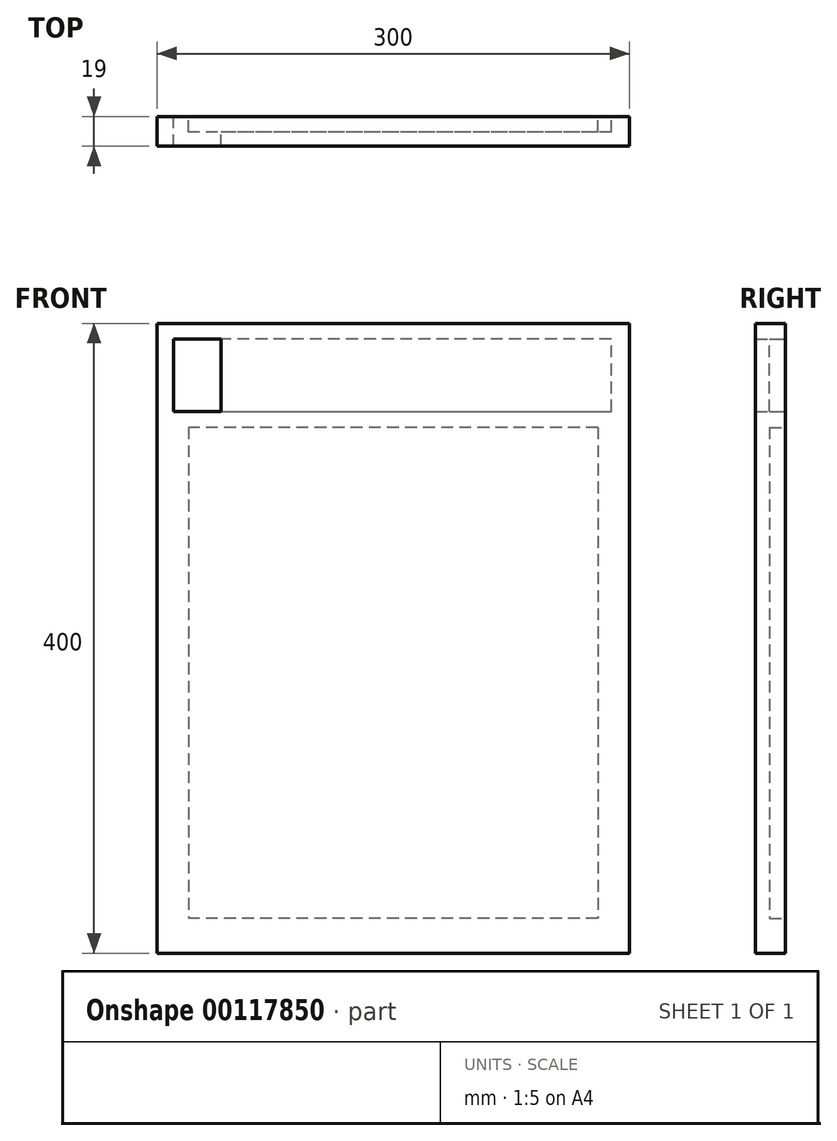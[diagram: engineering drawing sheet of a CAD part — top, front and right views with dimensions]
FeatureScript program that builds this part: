
annotation { "Feature Type Name" : "Feature", "Feature Type Description" : "" }
export const myFeature = defineFeature(function(context is Context, id is Id, definition is map)
    precondition{}
    {
        {
            var Q0;
            Q0=qCreatedBy(makeId("Front.planeOp"),FACE);
            var sketch = newSketch(context, id + "F0", { "sketchPlane" : qUnion([Q0])});
            skLineSegment(sketch, "E0.bottom", {"start": v(-158.35, 389.36) * mm, "end": v(141.65, 389.36) * mm});
            skLineSegment(sketch, "E0.top", {"start": v(-158.35, -10.64) * mm, "end": v(141.65, -10.64) * mm});
            skLineSegment(sketch, "E0.left", {"start": v(-158.35, 389.36) * mm, "end": v(-158.35, -10.64) * mm});
            skLineSegment(sketch, "E0.right", {"start": v(141.65, 389.36) * mm, "end": v(141.65, -10.64) * mm});
            skSolve(sketch);
        }
        {
            var Q0;
            Q0 = qSketchRegion(id + "F0", true);
            extrude(context, id + "F1", {"entities" : qUnion([Q0]), "depth" : 19 * mm});
        }
        {
            var Q0;
            Q0=makeQuery(id+"F1.opExtrude","CAP_FACE",FACE,{"disambiguationData":[OSD([sQuery(id+"F0.wireOp",EDGE,"E0.bottom"),sQuery(id+"F0.wireOp",EDGE,"E0.top"),sQuery(id+"F0.wireOp",EDGE,"E0.left"),sQuery(id+"F0.wireOp",EDGE,"E0.right")])],"isStart":true});
            var sketch = newSketch(context, id + "F2", { "sketchPlane" : qUnion([Q0])});
            skLineSegment(sketch, "E1", {"start": v(147.85, 379.36) * mm, "end": v(147.85, 333.36) * mm});
            skLineSegment(sketch, "E2", {"start": v(147.85, 333.36) * mm, "end": v(-130.15, 333.36) * mm});
            skLineSegment(sketch, "E3", {"start": v(-130.15, 333.36) * mm, "end": v(-130.15, 379.36) * mm});
            skLineSegment(sketch, "E4", {"start": v(-130.15, 379.36) * mm, "end": v(147.85, 379.36) * mm});
            skSolve(sketch);
        }
        {
            var Q0;
            Q0 = qSketchRegion(id + "F2", true);
            extrude(context, id + "F3", {"entities" : qUnion([Q0]), "operationType" : NewBodyOperationType.REMOVE, "oppositeDirection" : true, "depth" : 10 * mm});
        }
        {
            var Q0;
            Q0=makeQuery(id+"F3.boolean.opBoolean","COPY",FACE,{"derivedFrom":makeQuery(id+"F3.opExtrude","CAP_FACE",FACE,{"disambiguationData":[OSD([sQuery(id+"F2.wireOp",EDGE,"E1"),sQuery(id+"F2.wireOp",EDGE,"E2"),sQuery(id+"F2.wireOp",EDGE,"E3"),sQuery(id+"F2.wireOp",EDGE,"E4")])],"isStart":false})});
            var sketch = newSketch(context, id + "F4", { "sketchPlane" : qUnion([Q0])});
            skLineSegment(sketch, "E5.bottom", {"start": v(147.85, 379.36) * mm, "end": v(117.85, 379.36) * mm});
            skLineSegment(sketch, "E5.top", {"start": v(147.85, 333.36) * mm, "end": v(117.85, 333.36) * mm});
            skLineSegment(sketch, "E5.left", {"start": v(147.85, 379.36) * mm, "end": v(147.85, 333.36) * mm});
            skLineSegment(sketch, "E5.right", {"start": v(117.85, 379.36) * mm, "end": v(117.85, 333.36) * mm});
            skSolve(sketch);
        }
        {
            var Q0;
            Q0 = qSketchRegion(id + "F4", true);
            extrude(context, id + "F5", {"entities" : qUnion([Q0]), "operationType" : NewBodyOperationType.REMOVE, "oppositeDirection" : true, "depth" : 10 * mm});
        }
        {
            var Q0;
            Q0=makeQuery(id+"F1.opExtrude","CAP_FACE",FACE,{"disambiguationData":[OSD([sQuery(id+"F0.wireOp",EDGE,"E0.bottom"),sQuery(id+"F0.wireOp",EDGE,"E0.top"),sQuery(id+"F0.wireOp",EDGE,"E0.left"),sQuery(id+"F0.wireOp",EDGE,"E0.right")])],"isStart":true});
            var sketch = newSketch(context, id + "F6", { "sketchPlane" : qUnion([Q0])});
            skLineSegment(sketch, "E6.bottom", {"start": v(-121.65, 323.36) * mm, "end": v(138.35, 323.36) * mm});
            skLineSegment(sketch, "E6.top", {"start": v(-121.65, 11.36) * mm, "end": v(138.35, 11.36) * mm});
            skLineSegment(sketch, "E6.left", {"start": v(-121.65, 323.36) * mm, "end": v(-121.65, 11.36) * mm});
            skLineSegment(sketch, "E6.right", {"start": v(138.35, 323.36) * mm, "end": v(138.35, 11.36) * mm});
            skSolve(sketch);
        }
        {
            var Q0;
            Q0 = qSketchRegion(id + "F6", true);
            extrude(context, id + "F7", {"entities" : qUnion([Q0]), "operationType" : NewBodyOperationType.REMOVE, "oppositeDirection" : true, "depth" : 10 * mm});
        }
    });
